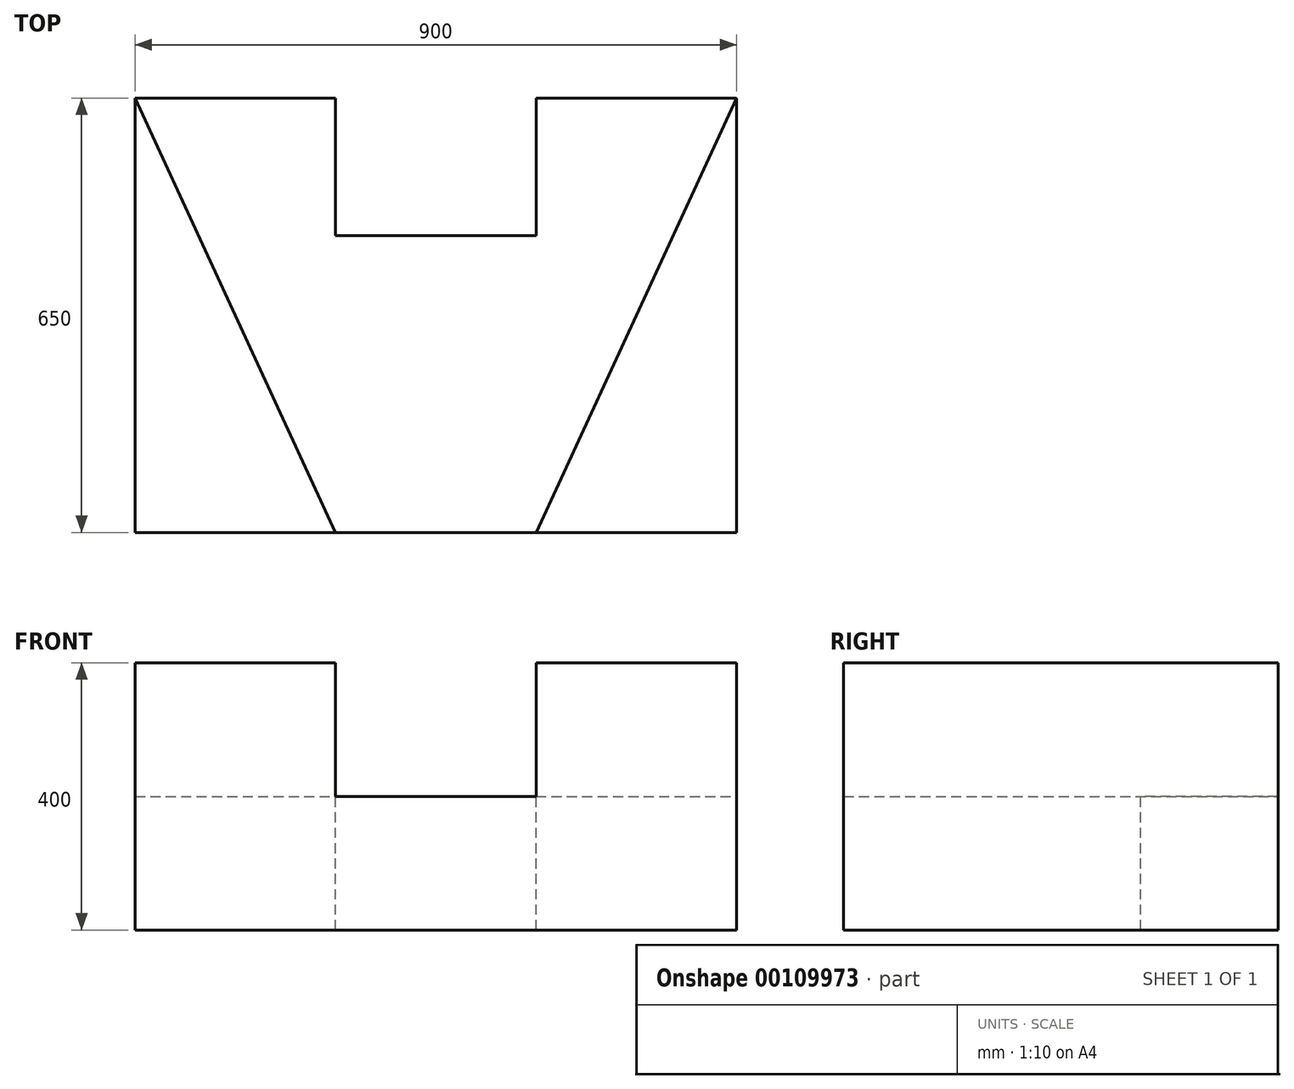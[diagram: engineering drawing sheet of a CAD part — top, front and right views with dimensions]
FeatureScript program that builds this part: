
annotation { "Feature Type Name" : "Feature", "Feature Type Description" : "" }
export const myFeature = defineFeature(function(context is Context, id is Id, definition is map)
    precondition{}
    {
        {
            var Q0;
            Q0=qCreatedBy(makeId("Top.planeOp"),FACE);
            var sketch = newSketch(context, id + "F0", { "sketchPlane" : qUnion([Q0])});
            skLineSegment(sketch, "E0.bottom", {"start": v(-417.48, 237.26) * mm, "end": v(482.52, 237.26) * mm});
            skLineSegment(sketch, "E0.top", {"start": v(-417.48, -412.74) * mm, "end": v(482.52, -412.74) * mm});
            skLineSegment(sketch, "E0.left", {"start": v(-417.48, 237.26) * mm, "end": v(-417.48, -412.74) * mm});
            skLineSegment(sketch, "E0.right", {"start": v(482.52, 237.26) * mm, "end": v(482.52, -412.74) * mm});
            skSolve(sketch);
        }
        {
            var Q0;
            Q0 = qSketchRegion(id + "F0", true);
            extrude(context, id + "F1", {"entities" : qUnion([Q0]), "depth" : 200 * mm});
        }
        {
            var Q0;
            Q0=makeQuery(id+"F1.opExtrude","CAP_FACE",FACE,{"disambiguationData":[OSD([sQuery(id+"F0.wireOp",EDGE,"E0.bottom"),sQuery(id+"F0.wireOp",EDGE,"E0.top"),sQuery(id+"F0.wireOp",EDGE,"E0.left"),sQuery(id+"F0.wireOp",EDGE,"E0.right")])],"isStart":false});
            var sketch = newSketch(context, id + "F2", { "sketchPlane" : qUnion([Q0])});
            skLineSegment(sketch, "E1", {"start": v(-417.48, 237.26) * mm, "end": v(-417.48, -412.74) * mm});
            skLineSegment(sketch, "E2", {"start": v(-417.48, -412.74) * mm, "end": v(-117.48, -412.74) * mm});
            skLineSegment(sketch, "E3", {"start": v(-117.48, -412.74) * mm, "end": v(-417.48, 237.26) * mm});
            skSolve(sketch);
        }
        {
            var Q0;
            Q0 = qSketchRegion(id + "F2", true);
            extrude(context, id + "F3", {"entities" : qUnion([Q0]), "operationType" : NewBodyOperationType.ADD, "depth" : 200 * mm});
        }
        {
            var Q0;
            Q0=makeQuery(id+"F1.opExtrude","CAP_FACE",FACE,{"disambiguationData":[OSD([sQuery(id+"F0.wireOp",EDGE,"E0.bottom"),sQuery(id+"F0.wireOp",EDGE,"E0.top"),sQuery(id+"F0.wireOp",EDGE,"E0.left"),sQuery(id+"F0.wireOp",EDGE,"E0.right")])],"isStart":false});
            var sketch = newSketch(context, id + "F4", { "sketchPlane" : qUnion([Q0])});
            skLineSegment(sketch, "E4", {"start": v(482.52, 237.26) * mm, "end": v(482.52, -412.74) * mm});
            skLineSegment(sketch, "E5", {"start": v(482.52, -412.74) * mm, "end": v(182.52, -412.74) * mm});
            skLineSegment(sketch, "E6", {"start": v(182.52, -412.74) * mm, "end": v(482.52, 237.26) * mm});
            skSolve(sketch);
        }
        {
            var Q0;
            Q0 = qSketchRegion(id + "F4", true);
            extrude(context, id + "F5", {"entities" : qUnion([Q0]), "operationType" : NewBodyOperationType.ADD, "depth" : 200 * mm});
        }
        {
            var Q0;
            Q0=makeQuery(id+"F1.opExtrude","CAP_FACE",FACE,{"disambiguationData":[OSD([sQuery(id+"F0.wireOp",EDGE,"E0.bottom"),sQuery(id+"F0.wireOp",EDGE,"E0.top"),sQuery(id+"F0.wireOp",EDGE,"E0.left"),sQuery(id+"F0.wireOp",EDGE,"E0.right")])],"isStart":false});
            var sketch = newSketch(context, id + "F6", { "sketchPlane" : qUnion([Q0])});
            skLineSegment(sketch, "E7.bottom", {"start": v(-117.48, 237.26) * mm, "end": v(182.52, 237.26) * mm});
            skLineSegment(sketch, "E7.top", {"start": v(-117.48, 31.73) * mm, "end": v(182.52, 31.73) * mm});
            skLineSegment(sketch, "E7.left", {"start": v(-117.48, 237.26) * mm, "end": v(-117.48, 31.73) * mm});
            skLineSegment(sketch, "E7.right", {"start": v(182.52, 237.26) * mm, "end": v(182.52, 31.73) * mm});
            skSolve(sketch);
        }
        {
            var Q0;
            Q0 = qSketchRegion(id + "F6", true);
            extrude(context, id + "F7", {"entities" : qUnion([Q0]), "operationType" : NewBodyOperationType.REMOVE, "oppositeDirection" : true, "depth" : 281.52 * mm});
        }
    });
